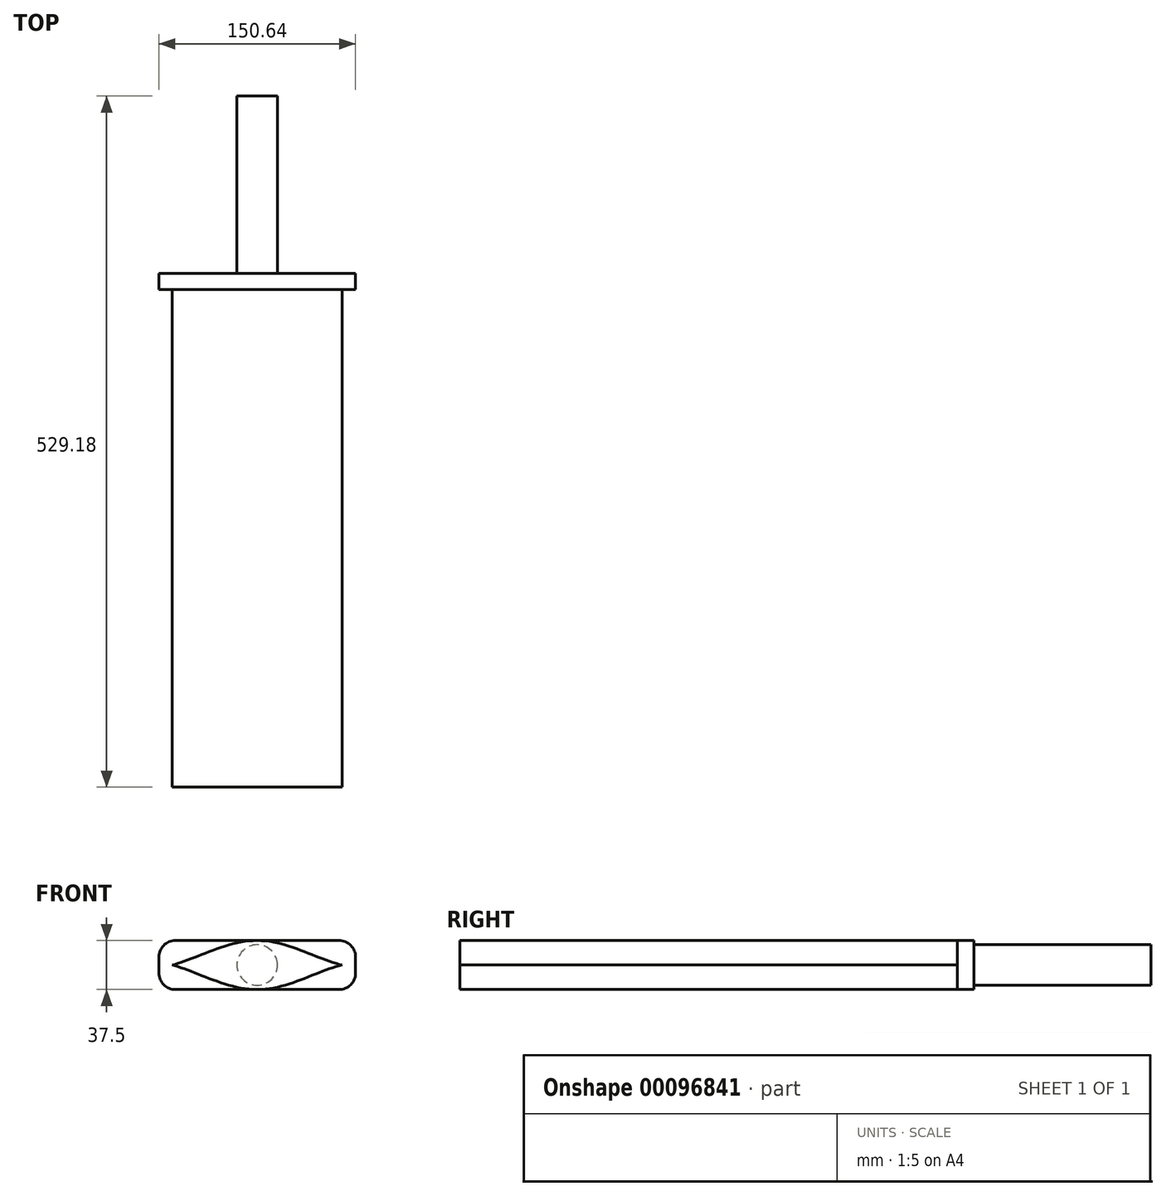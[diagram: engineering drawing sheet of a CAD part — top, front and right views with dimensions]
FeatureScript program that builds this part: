
annotation { "Feature Type Name" : "Feature", "Feature Type Description" : "" }
export const myFeature = defineFeature(function(context is Context, id is Id, definition is map)
    precondition{}
    {
        {
            var Q0;
            Q0=qCreatedBy(makeId("Front.planeOp"),FACE);
            var sketch = newSketch(context, id + "F0", { "sketchPlane" : qUnion([Q0])});
            skPoint(sketch, "E0.middle", {"position": v(0, 0) * mm});
            skLineSegment(sketch, "E1.bottom", {"start": v(-62.62, 18.75) * mm, "end": v(62.62, 18.75) * mm});
            skLineSegment(sketch, "E1.top", {"start": v(-62.62, -18.75) * mm, "end": v(62.62, -18.75) * mm});
            skLineSegment(sketch, "E1.left", {"start": v(-75.32, 6.05) * mm, "end": v(-75.32, -6.05) * mm});
            skLineSegment(sketch, "E1.right", {"start": v(75.32, 6.05) * mm, "end": v(75.32, -6.05) * mm});
            skCircle(sketch, "E2", {"center": v(0, 0) * mm, "radius": 15.52 * mm});
            skLineSegment(sketch, "E3", {"start": v(-75.32, 0) * mm, "end": v(-15.52, 0) * mm});
            skPoint(sketch, "E4.visualSharp", {"position": v(-75.32, 18.75) * mm});
            skArc(sketch, "E4.filletArc", {"start": v(-62.62, 18.75) * mm, "mid": v(-71.6, 15.03) * mm, "end": v(-75.32, 6.05) * mm});
            skPoint(sketch, "E5.visualSharp", {"position": v(-75.32, -18.75) * mm});
            skArc(sketch, "E5.filletArc", {"start": v(-75.32, -6.05) * mm, "mid": v(-71.6, -15.03) * mm, "end": v(-62.62, -18.75) * mm});
            skPoint(sketch, "E6.visualSharp", {"position": v(75.32, -18.75) * mm});
            skArc(sketch, "E6.filletArc", {"start": v(62.62, -18.75) * mm, "mid": v(71.6, -15.03) * mm, "end": v(75.32, -6.05) * mm});
            skPoint(sketch, "E7.visualSharp", {"position": v(75.32, 18.75) * mm});
            skArc(sketch, "E7.filletArc", {"start": v(75.32, 6.05) * mm, "mid": v(71.6, 15.03) * mm, "end": v(62.62, 18.75) * mm});
            skFitSpline(sketch, "E8", {"points": [v(-65.16, 0) * mm, v(0, 18.75) * mm, v(65.16, 0) * mm], "startDerivative": vector(99, 22.96) * mm, "endDerivative": vector(107.7, -22.53) * mm});
            skFitSpline(sketch, "E9.MirrorCS", {"points": [v(-65.16, 0) * mm, v(0, -18.75) * mm, v(65.16, 0) * mm], "startDerivative": vector(99, -22.96) * mm, "endDerivative": vector(107.7, 22.53) * mm});
            skLineSegment(sketch, "E10.trimOffspring", {"start": v(15.52, 0) * mm, "end": v(75.32, 0) * mm});
            skSolve(sketch);
        }
        {
            var Q0;
            {var subQ0=sQuery(id+"F0.wireOp",EDGE,"QxGuFVPm-JRUa-oWRD-hF52-c5ZJxIJQKKxb");var subQ1=sQuery(id+"F0.wireOp",EDGE,"E2");var subQ2=makeQuery(id+"F0.imprint","INTERSECT",VERTEX,{"disambiguationData":[OD(0.0)],"derivedFrom":[subQ1,subQ0]});Q0=makeQuery(id+"F0.imprint","IMPRINT",FACE,{"disambiguationData":[TD([[makeQuery(id+"F0.imprint","IMPRINT",EDGE,{"disambiguationData":[TD([[subQ2,-1.0]])],"derivedFrom":subQ1}),1.0]])]});}
            var Q1;
            {var subQ3=sQuery(id+"F0.wireOp",EDGE,"E2");var subQ5=sQuery(id+"F0.wireOp",EDGE,"QxGuFVPm-JRUa-oWRD-hF52-c5ZJxIJQKKxb");var subQ6=makeQuery(id+"F0.imprint","INTERSECT",VERTEX,{"disambiguationData":[OD(0.0)],"derivedFrom":[subQ3,subQ5]});Q1=makeQuery(id+"F0.imprint","IMPRINT",FACE,{"disambiguationData":[TD([[makeQuery(id+"F0.imprint","IMPRINT",EDGE,{"disambiguationData":[TD([[subQ6,-1.0]])],"derivedFrom":subQ3}),-1.0]])]});}
            var Q2;
            {var subQ4=sQuery(id+"F0.wireOp",EDGE,"E2");var subQ6=sQuery(id+"F0.wireOp",EDGE,"E3");var subQ7=makeQuery(id+"F0.imprint","INTERSECT",VERTEX,{"disambiguationData":[OD(1.0)],"derivedFrom":[subQ4,subQ6]});Q2=makeQuery(id+"F0.imprint","IMPRINT",FACE,{"disambiguationData":[TD([[makeQuery(id+"F0.imprint","IMPRINT",EDGE,{"disambiguationData":[TD([[subQ7,-1.0]])],"derivedFrom":subQ4}),-1.0]])]});}
            var Q3;
            {var subQ0=sQuery(id+"F0.wireOp",EDGE,"E3");var subQ1=sQuery(id+"F0.wireOp",EDGE,"E2");var subQ2=makeQuery(id+"F0.imprint","INTERSECT",VERTEX,{"disambiguationData":[OD(1.0)],"derivedFrom":[subQ1,subQ0]});Q3=makeQuery(id+"F0.imprint","IMPRINT",FACE,{"disambiguationData":[TD([[makeQuery(id+"F0.imprint","IMPRINT",EDGE,{"disambiguationData":[TD([[subQ2,-1.0]])],"derivedFrom":subQ1}),1.0]])]});}
            var Q4;
            {var subQ0=sQuery(id+"F0.wireOp",EDGE,"E3");var subQ1=sQuery(id+"F0.wireOp",EDGE,"E2");var subQ2=makeQuery(id+"F0.imprint","INTERSECT",VERTEX,{"disambiguationData":[OD(0.0)],"derivedFrom":[subQ1,subQ0]});Q4=makeQuery(id+"F0.imprint","IMPRINT",FACE,{"disambiguationData":[TD([[makeQuery(id+"F0.imprint","IMPRINT",EDGE,{"disambiguationData":[TD([[subQ2,1.0]])],"derivedFrom":subQ1}),1.0]])]});}
            var Q5;
            {var subQ0=sQuery(id+"F0.wireOp",EDGE,"QxGuFVPm-JRUa-oWRD-hF52-c5ZJxIJQKKxb");var subQ1=sQuery(id+"F0.wireOp",EDGE,"E2");var subQ2=makeQuery(id+"F0.imprint","INTERSECT",VERTEX,{"disambiguationData":[OD(0.0)],"derivedFrom":[subQ1,subQ0]});Q5=makeQuery(id+"F0.imprint","IMPRINT",FACE,{"disambiguationData":[TD([[makeQuery(id+"F0.imprint","IMPRINT",EDGE,{"disambiguationData":[TD([[subQ2,1.0]])],"derivedFrom":subQ1}),1.0]])]});}
            var Q6;
            {var subQ0=sQuery(id+"F0.wireOp",EDGE,"QxGuFVPm-JRUa-oWRD-hF52-c5ZJxIJQKKxb");var subQ1=sQuery(id+"F0.wireOp",EDGE,"E2");var subQ2=makeQuery(id+"F0.imprint","INTERSECT",VERTEX,{"disambiguationData":[OD(0.0)],"derivedFrom":[subQ1,subQ0]});Q6=makeQuery(id+"F0.imprint","IMPRINT",FACE,{"disambiguationData":[TD([[makeQuery(id+"F0.imprint","IMPRINT",EDGE,{"disambiguationData":[TD([[subQ2,1.0]])],"derivedFrom":subQ1}),-1.0]])]});}
            var Q7;
            {var subQ0=sQuery(id+"F0.wireOp",EDGE,"E3");var subQ1=sQuery(id+"F0.wireOp",EDGE,"E2");var subQ2=makeQuery(id+"F0.imprint","INTERSECT",VERTEX,{"disambiguationData":[OD(0.0)],"derivedFrom":[subQ1,subQ0]});Q7=makeQuery(id+"F0.imprint","IMPRINT",FACE,{"disambiguationData":[TD([[makeQuery(id+"F0.imprint","IMPRINT",EDGE,{"disambiguationData":[TD([[subQ2,1.0]])],"derivedFrom":subQ1}),-1.0]])]});}
            var Q8;
            {var subQ0=sQuery(id+"F0.wireOp",EDGE,"E7.filletArc");Q8=makeQuery(id+"F0.imprint","IMPRINT",FACE,{"disambiguationData":[TD([[makeQuery(id+"F0.imprint","IMPRINT",EDGE,{"derivedFrom":subQ0}),1.0]])]});}
            var Q9;
            {var subQ0=sQuery(id+"F0.wireOp",EDGE,"E4.filletArc");Q9=makeQuery(id+"F0.imprint","IMPRINT",FACE,{"disambiguationData":[TD([[makeQuery(id+"F0.imprint","IMPRINT",EDGE,{"derivedFrom":subQ0}),1.0]])]});}
            var Q10;
            {var subQ0=sQuery(id+"F0.wireOp",EDGE,"E5.filletArc");Q10=makeQuery(id+"F0.imprint","IMPRINT",FACE,{"disambiguationData":[TD([[makeQuery(id+"F0.imprint","IMPRINT",EDGE,{"derivedFrom":subQ0}),1.0]])]});}
            var Q11;
            {var subQ5=sQuery(id+"F0.wireOp",EDGE,"E6.filletArc");Q11=makeQuery(id+"F0.imprint","IMPRINT",FACE,{"disambiguationData":[TD([[makeQuery(id+"F0.imprint","IMPRINT",EDGE,{"derivedFrom":subQ5}),1.0]])]});}
            extrude(context, id + "F1", {"entities" : qUnion([Q0, Q1, Q2, Q3, Q4, Q5, Q6, Q7, Q8, Q9, Q10, Q11]), "oppositeDirection" : true, "depth" : 12.54 * mm});
        }
        {
            var Q0;
            {var subQ0=sQuery(id+"F0.wireOp",EDGE,"E3");var subQ1=sQuery(id+"F0.wireOp",EDGE,"E2");var subQ2=makeQuery(id+"F0.imprint","INTERSECT",VERTEX,{"disambiguationData":[OD(1.0)],"derivedFrom":[subQ1,subQ0]});Q0=makeQuery(id+"F0.imprint","IMPRINT",FACE,{"disambiguationData":[TD([[makeQuery(id+"F0.imprint","IMPRINT",EDGE,{"disambiguationData":[TD([[subQ2,-1.0]])],"derivedFrom":subQ1}),1.0]])]});}
            var Q1;
            {var subQ0=sQuery(id+"F0.wireOp",EDGE,"QxGuFVPm-JRUa-oWRD-hF52-c5ZJxIJQKKxb");var subQ1=sQuery(id+"F0.wireOp",EDGE,"E2");var subQ2=makeQuery(id+"F0.imprint","INTERSECT",VERTEX,{"disambiguationData":[OD(0.0)],"derivedFrom":[subQ1,subQ0]});Q1=makeQuery(id+"F0.imprint","IMPRINT",FACE,{"disambiguationData":[TD([[makeQuery(id+"F0.imprint","IMPRINT",EDGE,{"disambiguationData":[TD([[subQ2,-1.0]])],"derivedFrom":subQ1}),1.0]])]});}
            var Q2;
            {var subQ0=sQuery(id+"F0.wireOp",EDGE,"QxGuFVPm-JRUa-oWRD-hF52-c5ZJxIJQKKxb");var subQ1=sQuery(id+"F0.wireOp",EDGE,"E2");var subQ2=makeQuery(id+"F0.imprint","INTERSECT",VERTEX,{"disambiguationData":[OD(0.0)],"derivedFrom":[subQ1,subQ0]});Q2=makeQuery(id+"F0.imprint","IMPRINT",FACE,{"disambiguationData":[TD([[makeQuery(id+"F0.imprint","IMPRINT",EDGE,{"disambiguationData":[TD([[subQ2,1.0]])],"derivedFrom":subQ1}),1.0]])]});}
            var Q3;
            {var subQ0=sQuery(id+"F0.wireOp",EDGE,"E3");var subQ1=sQuery(id+"F0.wireOp",EDGE,"E2");var subQ2=makeQuery(id+"F0.imprint","INTERSECT",VERTEX,{"disambiguationData":[OD(0.0)],"derivedFrom":[subQ1,subQ0]});Q3=makeQuery(id+"F0.imprint","IMPRINT",FACE,{"disambiguationData":[TD([[makeQuery(id+"F0.imprint","IMPRINT",EDGE,{"disambiguationData":[TD([[subQ2,1.0]])],"derivedFrom":subQ1}),1.0]])]});}
            extrude(context, id + "F2", {"entities" : qUnion([Q0, Q1, Q2, Q3]), "operationType" : NewBodyOperationType.ADD, "oppositeDirection" : true, "depth" : 148.18 * mm});
        }
        {
            var Q0;
            {var subQ3=sQuery(id+"F0.wireOp",EDGE,"E2");var subQ5=sQuery(id+"F0.wireOp",EDGE,"QxGuFVPm-JRUa-oWRD-hF52-c5ZJxIJQKKxb");var subQ6=makeQuery(id+"F0.imprint","INTERSECT",VERTEX,{"disambiguationData":[OD(0.0)],"derivedFrom":[subQ3,subQ5]});Q0=makeQuery(id+"F0.imprint","IMPRINT",FACE,{"disambiguationData":[TD([[makeQuery(id+"F0.imprint","IMPRINT",EDGE,{"disambiguationData":[TD([[subQ6,-1.0]])],"derivedFrom":subQ3}),-1.0]])]});}
            var Q1;
            {var subQ0=sQuery(id+"F0.wireOp",EDGE,"QxGuFVPm-JRUa-oWRD-hF52-c5ZJxIJQKKxb");var subQ1=sQuery(id+"F0.wireOp",EDGE,"E2");var subQ2=makeQuery(id+"F0.imprint","INTERSECT",VERTEX,{"disambiguationData":[OD(0.0)],"derivedFrom":[subQ1,subQ0]});Q1=makeQuery(id+"F0.imprint","IMPRINT",FACE,{"disambiguationData":[TD([[makeQuery(id+"F0.imprint","IMPRINT",EDGE,{"disambiguationData":[TD([[subQ2,1.0]])],"derivedFrom":subQ1}),-1.0]])]});}
            var Q2;
            {var subQ0=sQuery(id+"F0.wireOp",EDGE,"E3");var subQ1=sQuery(id+"F0.wireOp",EDGE,"E2");var subQ2=makeQuery(id+"F0.imprint","INTERSECT",VERTEX,{"disambiguationData":[OD(0.0)],"derivedFrom":[subQ1,subQ0]});Q2=makeQuery(id+"F0.imprint","IMPRINT",FACE,{"disambiguationData":[TD([[makeQuery(id+"F0.imprint","IMPRINT",EDGE,{"disambiguationData":[TD([[subQ2,1.0]])],"derivedFrom":subQ1}),-1.0]])]});}
            var Q3;
            {var subQ4=sQuery(id+"F0.wireOp",EDGE,"E2");var subQ6=sQuery(id+"F0.wireOp",EDGE,"E3");var subQ7=makeQuery(id+"F0.imprint","INTERSECT",VERTEX,{"disambiguationData":[OD(1.0)],"derivedFrom":[subQ4,subQ6]});Q3=makeQuery(id+"F0.imprint","IMPRINT",FACE,{"disambiguationData":[TD([[makeQuery(id+"F0.imprint","IMPRINT",EDGE,{"disambiguationData":[TD([[subQ7,-1.0]])],"derivedFrom":subQ4}),-1.0]])]});}
            var Q4;
            {var subQ0=sQuery(id+"F0.wireOp",EDGE,"E3");var subQ1=sQuery(id+"F0.wireOp",EDGE,"E2");var subQ2=makeQuery(id+"F0.imprint","INTERSECT",VERTEX,{"disambiguationData":[OD(1.0)],"derivedFrom":[subQ1,subQ0]});Q4=makeQuery(id+"F0.imprint","IMPRINT",FACE,{"disambiguationData":[TD([[makeQuery(id+"F0.imprint","IMPRINT",EDGE,{"disambiguationData":[TD([[subQ2,-1.0]])],"derivedFrom":subQ1}),1.0]])]});}
            var Q5;
            {var subQ0=sQuery(id+"F0.wireOp",EDGE,"QxGuFVPm-JRUa-oWRD-hF52-c5ZJxIJQKKxb");var subQ1=sQuery(id+"F0.wireOp",EDGE,"E2");var subQ2=makeQuery(id+"F0.imprint","INTERSECT",VERTEX,{"disambiguationData":[OD(0.0)],"derivedFrom":[subQ1,subQ0]});Q5=makeQuery(id+"F0.imprint","IMPRINT",FACE,{"disambiguationData":[TD([[makeQuery(id+"F0.imprint","IMPRINT",EDGE,{"disambiguationData":[TD([[subQ2,1.0]])],"derivedFrom":subQ1}),1.0]])]});}
            var Q6;
            {var subQ0=sQuery(id+"F0.wireOp",EDGE,"QxGuFVPm-JRUa-oWRD-hF52-c5ZJxIJQKKxb");var subQ1=sQuery(id+"F0.wireOp",EDGE,"E2");var subQ2=makeQuery(id+"F0.imprint","INTERSECT",VERTEX,{"disambiguationData":[OD(0.0)],"derivedFrom":[subQ1,subQ0]});Q6=makeQuery(id+"F0.imprint","IMPRINT",FACE,{"disambiguationData":[TD([[makeQuery(id+"F0.imprint","IMPRINT",EDGE,{"disambiguationData":[TD([[subQ2,-1.0]])],"derivedFrom":subQ1}),1.0]])]});}
            var Q7;
            {var subQ0=sQuery(id+"F0.wireOp",EDGE,"E3");var subQ1=sQuery(id+"F0.wireOp",EDGE,"E2");var subQ2=makeQuery(id+"F0.imprint","INTERSECT",VERTEX,{"disambiguationData":[OD(0.0)],"derivedFrom":[subQ1,subQ0]});Q7=makeQuery(id+"F0.imprint","IMPRINT",FACE,{"disambiguationData":[TD([[makeQuery(id+"F0.imprint","IMPRINT",EDGE,{"disambiguationData":[TD([[subQ2,1.0]])],"derivedFrom":subQ1}),1.0]])]});}
            extrude(context, id + "F3", {"entities" : qUnion([Q0, Q1, Q2, Q3, Q4, Q5, Q6, Q7]), "operationType" : NewBodyOperationType.ADD, "depth" : 381 * mm});
        }
    });
